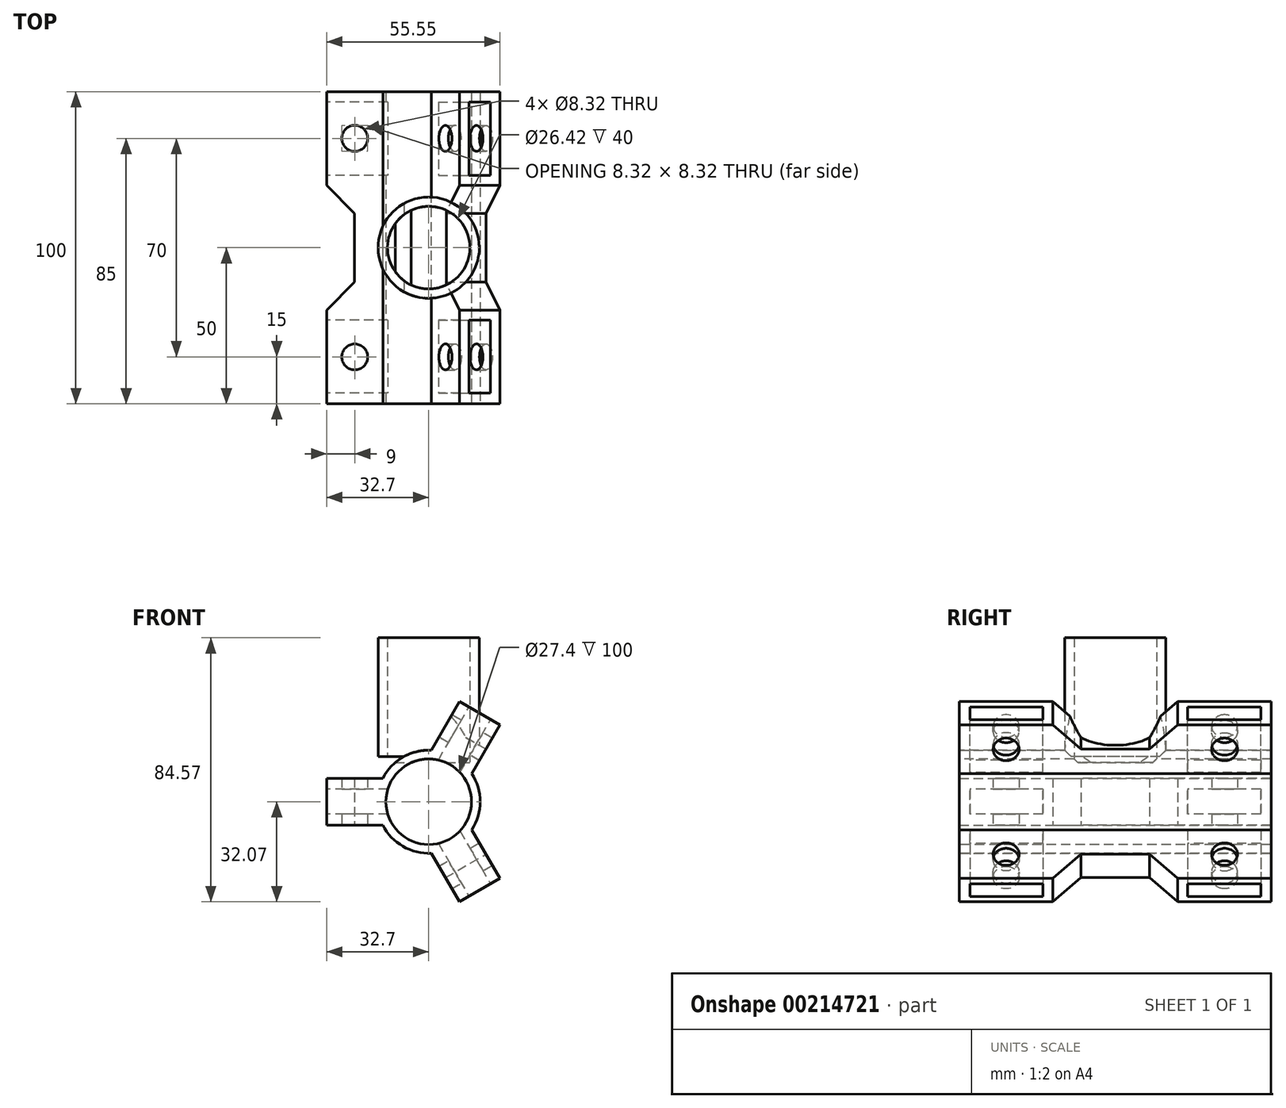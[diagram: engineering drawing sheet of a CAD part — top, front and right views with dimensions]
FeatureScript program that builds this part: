
annotation { "Feature Type Name" : "Feature", "Feature Type Description" : "" }
export const myFeature = defineFeature(function(context is Context, id is Id, definition is map)
    precondition{}
    {
        {
            var Q0;
            Q0=qCreatedBy(makeId("Top.planeOp"),FACE);
            var sketch = newSketch(context, id + "F0", { "sketchPlane" : qUnion([Q0])});
            skLineSegment(sketch, "E0", {"start": v(0, 0) * mm, "end": v(-12.7, 0) * mm, "construction": true});
            skLineSegment(sketch, "E1", {"start": v(-12.7, 0) * mm, "end": v(-12.7, 50) * mm, "construction": true});
            skLineSegment(sketch, "E2", {"start": v(-14.7, 0) * mm, "end": v(-14.7, 50) * mm});
            skLineSegment(sketch, "E3", {"start": v(-14.7, 0) * mm, "end": v(-32.7, 0) * mm});
            skLineSegment(sketch, "E4", {"start": v(-32.7, 0) * mm, "end": v(-32.7, 30) * mm});
            skLineSegment(sketch, "E5", {"start": v(-32.7, 30) * mm, "end": v(-14.7, 0) * mm, "construction": true});
            skLineSegment(sketch, "E6", {"start": v(-32.7, 0) * mm, "end": v(-14.7, 30) * mm, "construction": true});
            skCircle(sketch, "E7", {"center": v(-23.7, 15) * mm, "radius": 11 * mm, "construction": true});
            skCircle(sketch, "E8", {"center": v(-23.7, 15) * mm, "radius": 4.16 * mm});
            skLineSegment(sketch, "E9", {"start": v(-14.7, 39) * mm, "end": v(-23.75, 39) * mm, "construction": true});
            skLineSegment(sketch, "E10", {"start": v(-32.7, 30) * mm, "end": v(-23.75, 39) * mm});
            skLineSegment(sketch, "E11", {"start": v(-23.75, 39) * mm, "end": v(-23.75, 50) * mm});
            skLineSegment(sketch, "E12", {"start": v(-14.7, 50) * mm, "end": v(-23.75, 50) * mm, "construction": true});
            skLineSegment(sketch, "E13.MirrorCS", {"start": v(-23.75, 61) * mm, "end": v(-23.75, 50) * mm});
            skLineSegment(sketch, "E14.MirrorCS", {"start": v(-32.7, 70) * mm, "end": v(-23.75, 61) * mm});
            skLineSegment(sketch, "E15.MirrorCS", {"start": v(-32.7, 100) * mm, "end": v(-32.7, 70) * mm});
            skLineSegment(sketch, "E16.MirrorCS", {"start": v(-14.7, 100) * mm, "end": v(-32.7, 100) * mm});
            skLineSegment(sketch, "E17.MirrorCS", {"start": v(-14.7, 100) * mm, "end": v(-14.7, 50) * mm});
            skCircle(sketch, "E18.MirrorC", {"center": v(-23.7, 85) * mm, "radius": 4.16 * mm});
            skLineSegment(sketch, "E19.MirrorCS", {"start": v(-12.7, 100) * mm, "end": v(-12.7, 50) * mm, "construction": true});
            skCircle(sketch, "E20.MirrorC", {"center": v(-23.7, 85) * mm, "radius": 11 * mm, "construction": true});
            skSolve(sketch);
        }
        {
            var Q0;
            Q0=makeQuery(id+"F0.imprint","IMPRINT",FACE,{"disambiguationData":[TD([[makeQuery(id+"F0.imprint","IMPRINT",EDGE,{"derivedFrom":sQuery(id+"F0.wireOp",EDGE,"E2")}),1.0]])]});
            extrude(context, id + "F1", {"entities" : qUnion([Q0]), "depth" : 15 * mm});
        }
        {
            var Q0;
            Q0=makeQuery(id+"F1.opExtrude","SWEPT_FACE",FACE,{"disambiguationData":[OSD([sQuery(id+"F0.wireOp",EDGE,"E3")])]});
            var sketch = newSketch(context, id + "F2", { "sketchPlane" : qUnion([Q0])});
            skCircle(sketch, "E21", {"center": v(0, 7.5) * mm, "radius": 16.5 * mm, "construction": true});
            skCircle(sketch, "E22", {"center": v(0, 7.5) * mm, "radius": 13.7 * mm, "construction": true});
            skPoint(sketch, "E23.endSnap0", {"position": v(-14.7, 7.5) * mm});
            skLineSegment(sketch, "E24", {"start": v(0, 7.5) * mm, "end": v(-13.7, 7.5) * mm, "construction": true});
            skLineSegment(sketch, "E25", {"start": v(0, 7.5) * mm, "end": v(-6.85, -4.36) * mm, "construction": true});
            skLineSegment(sketch, "E26", {"start": v(0, 7.5) * mm, "end": v(-6.85, 19.36) * mm, "construction": true});
            skArc(sketch, "E27", {"start": v(-6.85, 19.36) * mm, "mid": v(-13.7, 7.5) * mm, "end": v(-6.85, -4.36) * mm});
            skLineSegment(sketch, "E28", {"start": v(-6.85, 19.36) * mm, "end": v(-8.25, 21.8) * mm});
            skLineSegment(sketch, "E29", {"start": v(-6.85, -4.36) * mm, "end": v(-8.25, -6.8) * mm});
            skCircle(sketch, "E30", {"center": v(0, 7.5) * mm, "radius": 12.7 * mm, "construction": true});
            skLineSegment(sketch, "E31", {"start": v(-13.7, 7.5) * mm, "end": v(-16.5, 7.5) * mm, "construction": true});
            skArc(sketch, "E32", {"start": v(-8.25, 21.8) * mm, "mid": v(-16.5, 7.5) * mm, "end": v(-8.25, -6.8) * mm});
            skSolve(sketch);
        }
        {
            var Q0;
            {var subQ0=sQuery(id+"F2.wireOp",EDGE,"E21");var subQ1=sQuery(id+"F0.wireOp",EDGE,"E3");var subQ2=makeQuery(id+"F1.opExtrude","SWEPT_EDGE",EDGE,{"disambiguationData":[OSD([sQuery(id+"F0.wireOp",EDGE,"E2"),subQ1])]});var subQ3=makeQuery(id+"F2.imprint","INTERSECT",VERTEX,{"derivedFrom":[subQ2,makeQuery(id+"F1.opExtrude","CAP_EDGE",EDGE,{"disambiguationData":[OSD([subQ1])],"isStart":true}),subQ0]});Q0=makeQuery(id+"F2.imprint","IMPRINT",FACE,{"disambiguationData":[TD([[makeQuery(id+"F2.imprint","IMPRINT",EDGE,{"disambiguationData":[TD([[subQ3,1.0]])],"derivedFrom":subQ0}),1.0]])]});}
            var Q1;
            {var subQ0=sQuery(id+"F2.wireOp",EDGE,"g3xJxAlq-R5pZ-Eeo2-CjEf-WmfwMOpCXLWw");Q1=makeQuery(id+"F2.imprint","IMPRINT",FACE,{"disambiguationData":[TD([[makeQuery(id+"F2.imprint","IMPRINT",EDGE,{"derivedFrom":subQ0}),-1.0]])]});}
            var Q2;
            Q2=makeQuery(id+"F2.imprint","IMPRINT",FACE,{"disambiguationData":[TD([[makeQuery(id+"F2.imprint","IMPRINT",EDGE,{"derivedFrom":sQuery(id+"F2.wireOp",EDGE,"E22")}),-1.0]])]});
            var Q3;
            Q3=makeQuery(id+"F2.imprint","IMPRINT",FACE,{"disambiguationData":[TD([[makeQuery(id+"F2.imprint","IMPRINT",EDGE,{"derivedFrom":sQuery(id+"F2.wireOp",EDGE,"E27")}),-1.0]])]});
            extrude(context, id + "F3", {"entities" : qUnion([Q0, Q1, Q2, Q3]), "operationType" : NewBodyOperationType.ADD, "oppositeDirection" : true, "depth" : 100 * mm});
        }
        {
            var Q0;
            Q0=makeQuery(id+"F1.opExtrude","SWEPT_FACE",FACE,{"disambiguationData":[OSD([sQuery(id+"F0.wireOp",EDGE,"E15.MirrorCS")])]});
            var sketch = newSketch(context, id + "F4", { "sketchPlane" : qUnion([Q0])});
            skLineSegment(sketch, "E33.bottom", {"start": v(-96.6, 11.5) * mm, "end": v(-73.2, 11.5) * mm});
            skLineSegment(sketch, "E33.top", {"start": v(-96.6, 3.5) * mm, "end": v(-73.2, 3.5) * mm});
            skLineSegment(sketch, "E33.left", {"start": v(-96.6, 11.5) * mm, "end": v(-96.6, 3.5) * mm});
            skLineSegment(sketch, "E33.right", {"start": v(-73.2, 11.5) * mm, "end": v(-73.2, 3.5) * mm});
            skLineSegment(sketch, "E34.bottom", {"start": v(-3.4, 3.5) * mm, "end": v(-26.8, 3.5) * mm});
            skLineSegment(sketch, "E34.top", {"start": v(-3.4, 11.5) * mm, "end": v(-26.8, 11.5) * mm});
            skLineSegment(sketch, "E34.left", {"start": v(-3.4, 3.5) * mm, "end": v(-3.4, 11.5) * mm});
            skLineSegment(sketch, "E34.right", {"start": v(-26.8, 3.5) * mm, "end": v(-26.8, 11.5) * mm});
            skSolve(sketch);
        }
        {
            var Q0;
            Q0=makeQuery(id+"F4.imprint","IMPRINT",FACE,{"disambiguationData":[TD([[makeQuery(id+"F4.imprint","IMPRINT",EDGE,{"derivedFrom":sQuery(id+"F4.wireOp",EDGE,"E33.bottom")}),-1.0]])]});
            var Q1;
            Q1=makeQuery(id+"F4.imprint","IMPRINT",FACE,{"disambiguationData":[TD([[makeQuery(id+"F4.imprint","IMPRINT",EDGE,{"derivedFrom":sQuery(id+"F4.wireOp",EDGE,"E34.bottom")}),-1.0]])]});
            extrude(context, id + "F5", {"entities" : qUnion([Q0, Q1]), "operationType" : NewBodyOperationType.REMOVE, "oppositeDirection" : true, "depth" : 25 * mm});
        }
        {
            var Q0;
            {var subQ0=sQuery(id+"F0.wireOp",EDGE,"E3");Q0=makeQuery(id+"F3.boolean.opBoolean","MERGE",FACE,{"derivedFrom":[makeQuery(id+"F1.opExtrude","SWEPT_FACE",FACE,{"disambiguationData":[OSD([subQ0])]}),makeQuery(id+"F3.opExtrude","CAP_FACE",FACE,{"disambiguationData":[OSD([sQuery(id+"F0.wireOp",EDGE,"E2"),subQ0,sQuery(id+"F2.wireOp",EDGE,"sGRMKCaJ-qwij-XAyk-PemZ-jGETvxKNh2jk"),sQuery(id+"F2.wireOp",EDGE,"E27"),sQuery(id+"F2.wireOp",EDGE,"E28"),sQuery(id+"F2.wireOp",EDGE,"E29")])],"isStart":true})]});}
            var sketch = newSketch(context, id + "F6", { "sketchPlane" : qUnion([Q0])});
            skCircle(sketch, "E35", {"center": v(0, 7.5) * mm, "radius": 13.7 * mm});
            skSolve(sketch);
        }
        {
            var Q0;
            Q0=makeQuery(id+"F1.opExtrude","SWEPT_BODY",BODY,{"disambiguationData":[OSD([sQuery(id+"F0.wireOp",EDGE,"E2"),sQuery(id+"F0.wireOp",EDGE,"E3"),sQuery(id+"F0.wireOp",EDGE,"E4"),sQuery(id+"F0.wireOp",EDGE,"E8"),sQuery(id+"F0.wireOp",EDGE,"E10"),sQuery(id+"F0.wireOp",EDGE,"E11"),sQuery(id+"F0.wireOp",EDGE,"E13.MirrorCS"),sQuery(id+"F0.wireOp",EDGE,"E14.MirrorCS"),sQuery(id+"F0.wireOp",EDGE,"E15.MirrorCS"),sQuery(id+"F0.wireOp",EDGE,"E16.MirrorCS"),sQuery(id+"F0.wireOp",EDGE,"E17.MirrorCS"),sQuery(id+"F0.wireOp",EDGE,"E18.MirrorC")])]});
            var Q1;
            Q1=sQuery(id+"F6.wireOp",EDGE,"E35");
            circularPattern(context, id + "F7", {"operationType" : NewBodyOperationType.ADD, "entities" : qUnion([Q0]), "axis" : qUnion([Q1]), "angle" : 360 * degree, "instanceCount" : 3, "equalSpace" : true, "computeTransformsWithoutBuiltin" : true});
        }
        {
            var Q0;
            Q0=qCreatedBy(makeId("Top.planeOp"),FACE);
            var sketch = newSketch(context, id + "F8", { "sketchPlane" : qUnion([Q0])});
            skCircle(sketch, "E36", {"center": v(0, 50) * mm, "radius": 13.2 * mm});
            skCircle(sketch, "E37", {"center": v(0, 50) * mm, "radius": 16.2 * mm});
            skSolve(sketch);
        }
        {
            var Q0;
            Q0=makeQuery(id+"F8.imprint","IMPRINT",FACE,{"disambiguationData":[TD([[makeQuery(id+"F8.imprint","IMPRINT",EDGE,{"derivedFrom":sQuery(id+"F8.wireOp",EDGE,"E36")}),-1.0]])]});
            extrude(context, id + "F9", {"entities" : qUnion([Q0]), "operationType" : NewBodyOperationType.ADD, "depth" : 60 * mm, "hasSecondDirection" : true, "secondDirectionOppositeDirection" : false, "secondDirectionDepth" : 22 * mm});
        }
        {
            var Q0;
            Q0=makeQuery(id+"F9.opExtrude","CAP_FACE",FACE,{"disambiguationData":[OSD([sQuery(id+"F8.wireOp",EDGE,"E36"),sQuery(id+"F8.wireOp",EDGE,"E37")])],"isStart":false});
            var sketch = newSketch(context, id + "F10", { "sketchPlane" : qUnion([Q0])});
            skCircle(sketch, "E38", {"center": v(0, 50) * mm, "radius": 12.7 * mm});
            skSolve(sketch);
        }
        {
            var Q0;
            Q0=makeQuery(id+"F10.imprint","IMPRINT",FACE,{"disambiguationData":[TD([[makeQuery(id+"F10.imprint","IMPRINT",EDGE,{"derivedFrom":sQuery(id+"F10.wireOp",EDGE,"E38")}),1.0]])]});
            extrude(context, id + "F11", {"entities" : qUnion([Q0]), "operationType" : NewBodyOperationType.REMOVE, "oppositeDirection" : true, "depth" : 40 * mm});
        }
        {
            var Q0;
            Q0=makeQuery(id+"F9.opExtrude","CAP_FACE",FACE,{"disambiguationData":[OSD([sQuery(id+"F8.wireOp",EDGE,"E36"),sQuery(id+"F8.wireOp",EDGE,"E37")])],"isStart":false});
            var sketch = newSketch(context, id + "F12", { "sketchPlane" : qUnion([Q0])});
            skCircle(sketch, "E39", {"center": v(0, 50) * mm, "radius": 13.2 * mm});
            skSolve(sketch);
        }
        {
            var Q0;
            Q0=makeQuery(id+"F12.imprint","IMPRINT",FACE,{"disambiguationData":[TD([[makeQuery(id+"F12.imprint","IMPRINT",EDGE,{"derivedFrom":sQuery(id+"F12.wireOp",EDGE,"E39")}),1.0]])]});
            extrude(context, id + "F13", {"entities" : qUnion([Q0]), "operationType" : NewBodyOperationType.REMOVE, "oppositeDirection" : true, "depth" : 40 * mm});
        }
    });
